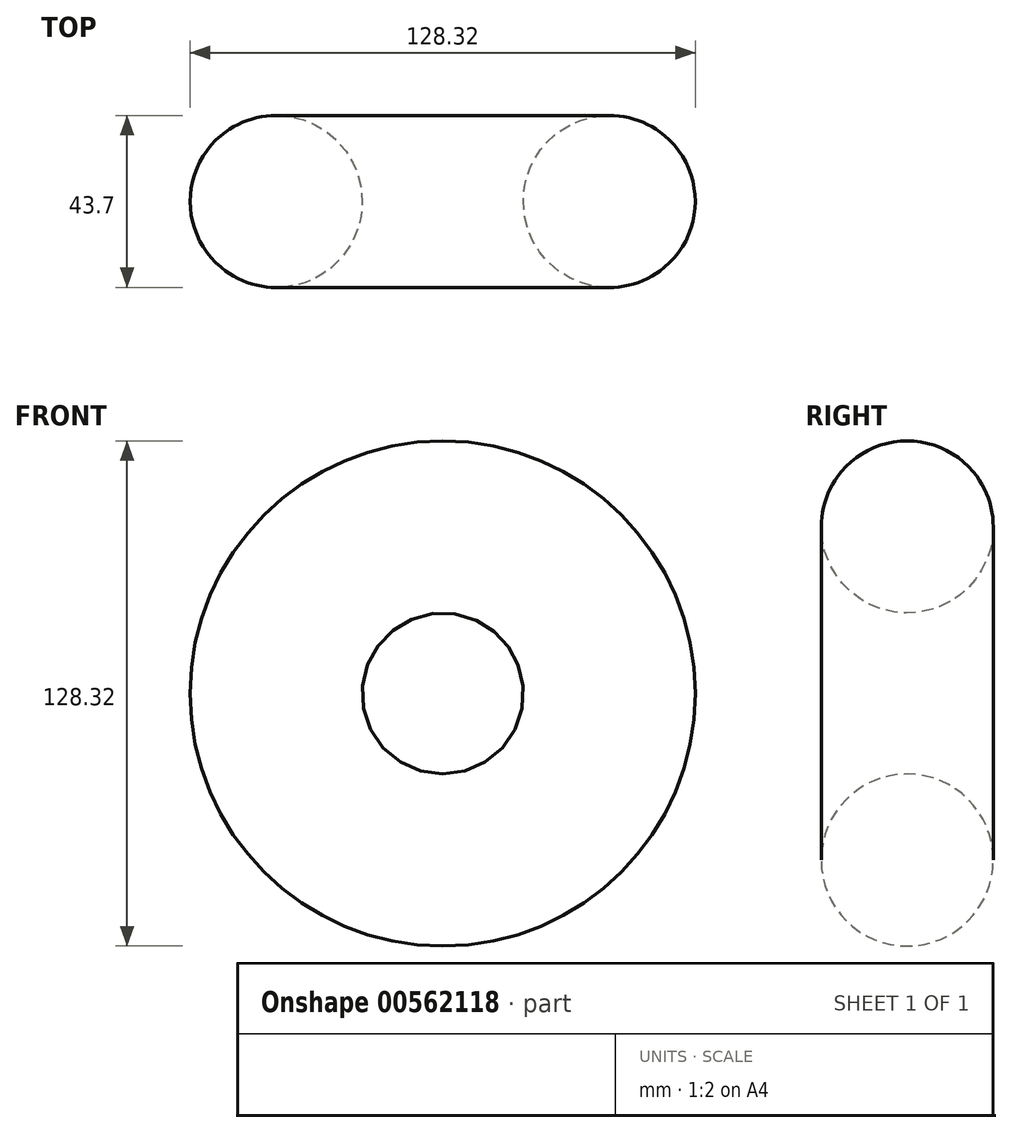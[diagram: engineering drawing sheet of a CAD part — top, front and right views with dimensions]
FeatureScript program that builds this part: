
annotation { "Feature Type Name" : "Feature", "Feature Type Description" : "" }
export const myFeature = defineFeature(function(context is Context, id is Id, definition is map)
    precondition{}
    {
        {
            var Q0;
            Q0=qCreatedBy(makeId("Top.planeOp"),FACE);
            var sketch = newSketch(context, id + "F0", { "sketchPlane" : qUnion([Q0])});
            skCircle(sketch, "E0", {"center": v(42.3, 33.1) * mm, "radius": 21.85 * mm});
            skLineSegment(sketch, "E1", {"start": v(0, 0) * mm, "end": v(0, 47.49) * mm, "construction": true});
            skSolve(sketch);
        }
        {
            var Q0;
            Q0=makeQuery(id+"F0.imprint","IMPRINT",FACE,{"disambiguationData":[TD([[makeQuery(id+"F0.imprint","IMPRINT",EDGE,{"derivedFrom":sQuery(id+"F0.wireOp",EDGE,"E0")}),1.0]])]});
            var Q1;
            Q1=sQuery(id+"F0.wireOp",EDGE,"E1");
            revolve(context, id + "F1", {"entities" : qUnion([Q0]), "axis" : qUnion([Q1]), "revolveType" : RevolveType.FULL});
        }
    });
